FCSTD DOCUMENT  (FreeCAD 0.18R16146 (Git))
Label: guitar_test
License: All rights reserved
LicenseURL: http://en.wikipedia.org/wiki/All_rights_reserved
objects: PartDesign::Body×2, Sketcher::SketchObject×1
note: 3 computed .brp shape members not serialized (recipe doc carries the construction recipe); baked Part::Feature solids carry a one-line shape summary decoded from their .brp

FEATURE [Sketcher::SketchObject] Sketch
  sketch-geometry (9):
    g0: ArcOfCircle CenterX=1.3e-15 CenterY=700 CenterZ=0 NormalX=0 NormalY=0 NormalZ=1 AngleXU=0 Radius=700 StartAngle=4.65879 EndAngle=4.76599
    g1: ArcOfCircle CenterX=30 CenterY=140.804 CenterZ=0 NormalX=0 NormalY=0 NormalZ=1 AngleXU=0 Radius=140 StartAngle=4.76599 EndAngle=7.23955
    g2: ArcOfCircle CenterX=145.299 CenterY=304.224 CenterZ=0 NormalX=0 NormalY=0 NormalZ=1 AngleXU=0 Radius=60 StartAngle=2.48842 EndAngle=4.09796
    g3: ArcOfCircle CenterX=50 CenterY=377.15 CenterZ=0 NormalX=0 NormalY=0 NormalZ=1 AngleXU=0 Radius=60 StartAngle=5.63001 EndAngle=7.7401
    g4: ArcOfCircle CenterX=-30 CenterY=140.804 CenterZ=0 NormalX=0 NormalY=0 NormalZ=1 AngleXU=0 Radius=140 StartAngle=2.18523 EndAngle=4.65879
    g5: ArcOfCircle CenterX=-145.299 CenterY=304.224 CenterZ=0 NormalX=0 NormalY=0 NormalZ=1 AngleXU=0 Radius=60 StartAngle=5.32682 EndAngle=6.93636
    g6: ArcOfCircle CenterX=-50 CenterY=377.15 CenterZ=0 NormalX=0 NormalY=0 NormalZ=1 AngleXU=0 Radius=60 StartAngle=1.68468 EndAngle=3.79477
    g7: ArcOfCircle CenterX=1.544e-13 CenterY=-60 CenterZ=0 NormalX=0 NormalY=0 NormalZ=1 AngleXU=0 Radius=500 StartAngle=1.45691 EndAngle=1.68468
    g8: GeomPoint X=0 Y=440 Z=0
  constraints (25):
    c: Tangent(g0,g1) = -1.5708  'Tangent1'
    c: Tangent(g1,g2) = 1.5708  'Tangent2'
    c: Tangent(g2,g3) = 1.5708  'Tangent3'
    c: Radius(g3) = 60  'Upper Bout Radius'
    c: Radius(g2) = 60  'Waist Radius'
    c: Radius(g1) = 140  'Lower Bout Radius'
    c: Radius(g0) = 700  'Bottom of Lower Bout Radius'
    c: Tangent(g4,g5) = 1.5708
    c: Tangent(g5,g6) = 1.5708
    c: Tangent(g0,g4) = -1.5708
    c: PointOnObject(g-1,g0)
    c: Symmetric(g6,g3,g-2)
    c: Symmetric(g4,g1,g-2)
    c: Symmetric(g0,g0,g-2)
    c: Symmetric(g5,g2,g-2)
    c: Symmetric(g2,g5,g-2)
    c: Tangent(g6,g7) = -1.5708
    c: Tangent(g3,g7) = -1.5708
    c: Radius(g7) = 500  'Top of Upper Bout Radius'
    c: Symmetric(g3,g6,g-2)
    c: DistanceX(g3) = 50
    c: DistanceX(g1) = 30
    c: PointOnObject(g8,g7)
    c: DistanceY(g8) = 440  'Body Height'
    c: DistanceX(g8) = 0
FEATURE [PartDesign::Body] Body
  Origin = -> Origin
FEATURE [PartDesign::Body] Body001
  Origin = -> Origin001
